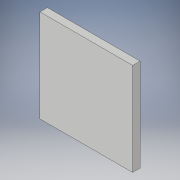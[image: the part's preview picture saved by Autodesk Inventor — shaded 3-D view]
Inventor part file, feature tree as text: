
AUTODESK INVENTOR PART (.ipt)
format: ipt  version: 2019 (Build 230136000, 136)  size: 89,088 bytes
history: native  units: mm
features: extrude x1, sketch x1
ambient origin geometry x8: Origin, YZ Plane, XZ Plane, XY Plane, X Axis, Y Axis, Z Axis, Center Point
bodies: Solid1 (feature_tree)
feature tree (2):
  extrude  "Extrusion1"  Depth=158.0mm
  sketch  "Sketch1"  dims[d0=158.0mm d1=158.0mm d2=12.7mm d3=0.0mm]
